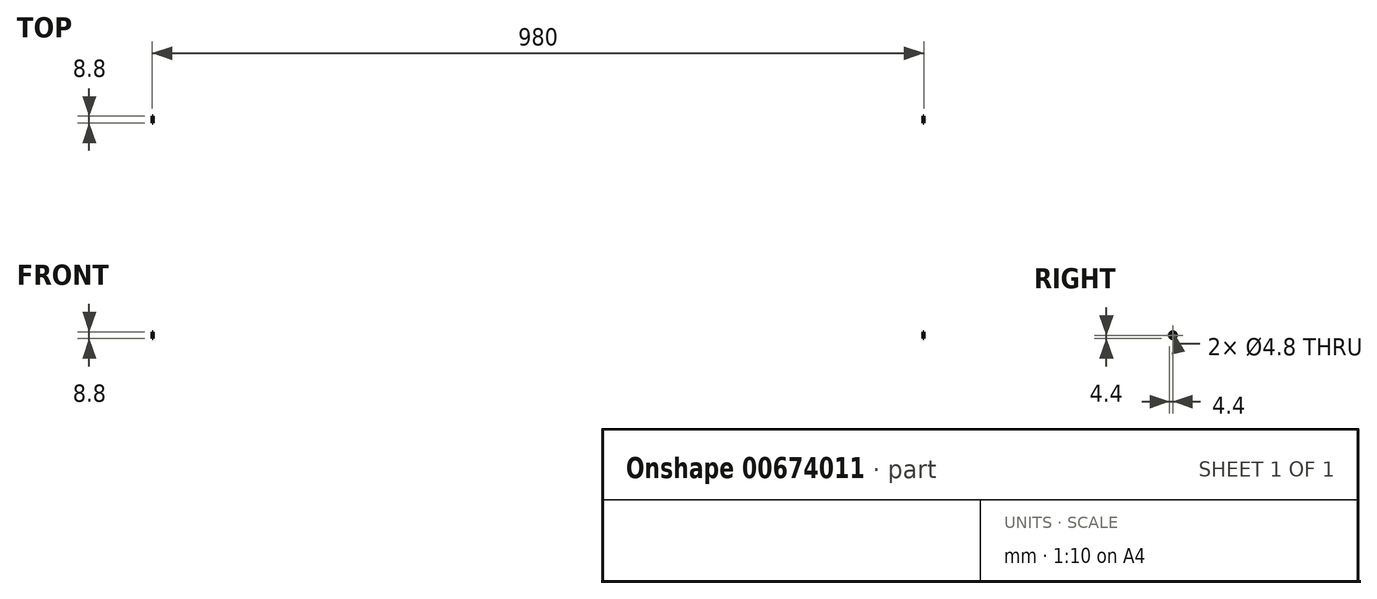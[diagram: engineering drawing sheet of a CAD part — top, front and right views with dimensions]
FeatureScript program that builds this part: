
annotation { "Feature Type Name" : "Feature", "Feature Type Description" : "" }
export const myFeature = defineFeature(function(context is Context, id is Id, definition is map)
    precondition{}
    {
        {
            var Q0;
            Q0=qCreatedBy(makeId("Front.planeOp"),FACE);
            var sketch = newSketch(context, id + "F0", { "sketchPlane" : qUnion([Q0])});
            skLineSegment(sketch, "E0.bottom", {"start": v(500, 1.2) * mm, "end": v(-500, 1.2) * mm});
            skLineSegment(sketch, "E0.top", {"start": v(500, -1.2) * mm, "end": v(-500, -1.2) * mm});
            skLineSegment(sketch, "E0.left", {"start": v(500, 1.2) * mm, "end": v(500, -1.2) * mm});
            skLineSegment(sketch, "E0.right", {"start": v(-500, 1.2) * mm, "end": v(-500, -1.2) * mm});
            skPoint(sketch, "E0.middle", {"position": v(0, 0) * mm});
            skLineSegment(sketch, "E1", {"start": v(-490, 1.2) * mm, "end": v(-490, 3.2) * mm});
            skLineSegment(sketch, "E2", {"start": v(-490, 3.2) * mm, "end": v(-489, 3.2) * mm});
            skLineSegment(sketch, "E3", {"start": v(-489, 3.2) * mm, "end": v(-489, 1.2) * mm});
            skLineSegment(sketch, "E4", {"start": v(-495.5, 1.2) * mm, "end": v(-495.5, 0.7) * mm});
            skLineSegment(sketch, "E5", {"start": v(-495.5, 0.7) * mm, "end": v(-497.5, 0.7) * mm});
            skLineSegment(sketch, "E6", {"start": v(-497.5, 0.7) * mm, "end": v(-497.5, 1.2) * mm});
            skLineSegment(sketch, "E7", {"start": v(490, 1.2) * mm, "end": v(490, 3.2) * mm});
            skLineSegment(sketch, "E8", {"start": v(490, 3.2) * mm, "end": v(489, 3.2) * mm});
            skLineSegment(sketch, "E9", {"start": v(489, 3.2) * mm, "end": v(489, 1.2) * mm});
            skLineSegment(sketch, "E10", {"start": v(495.5, 1.2) * mm, "end": v(495.5, 0.7) * mm});
            skLineSegment(sketch, "E11", {"start": v(495.5, 0.7) * mm, "end": v(497.5, 0.7) * mm});
            skLineSegment(sketch, "E12", {"start": v(497.5, 0.7) * mm, "end": v(497.5, 1.2) * mm});
            skSolve(sketch);
        }
        {
            var Q0;
            Q0=makeQuery(id+"F0.imprint","IMPRINT",FACE,{"disambiguationData":[TD([[makeQuery(id+"F0.imprint","IMPRINT",EDGE,{"derivedFrom":sQuery(id+"F0.wireOp",EDGE,"E0.top")}),-1.0]])]});
            var Q1;
            {var subQ0=sQuery(id+"F0.wireOp",EDGE,"E7");Q1=makeQuery(id+"F0.imprint","IMPRINT",FACE,{"disambiguationData":[TD([[makeQuery(id+"F0.imprint","IMPRINT",EDGE,{"derivedFrom":subQ0}),1.0]])]});}
            var Q2;
            {var subQ0=sQuery(id+"F0.wireOp",EDGE,"E1");Q2=makeQuery(id+"F0.imprint","IMPRINT",FACE,{"disambiguationData":[TD([[makeQuery(id+"F0.imprint","IMPRINT",EDGE,{"derivedFrom":subQ0}),-1.0]])]});}
            var Q3;
            Q3=sQuery(id+"F0.wireOp",EDGE,"E0.top");
            revolve(context, id + "F1", {"entities" : qUnion([Q0, Q1, Q2]), "axis" : qUnion([Q3]), "revolveType" : RevolveType.FULL});
        }
    });
